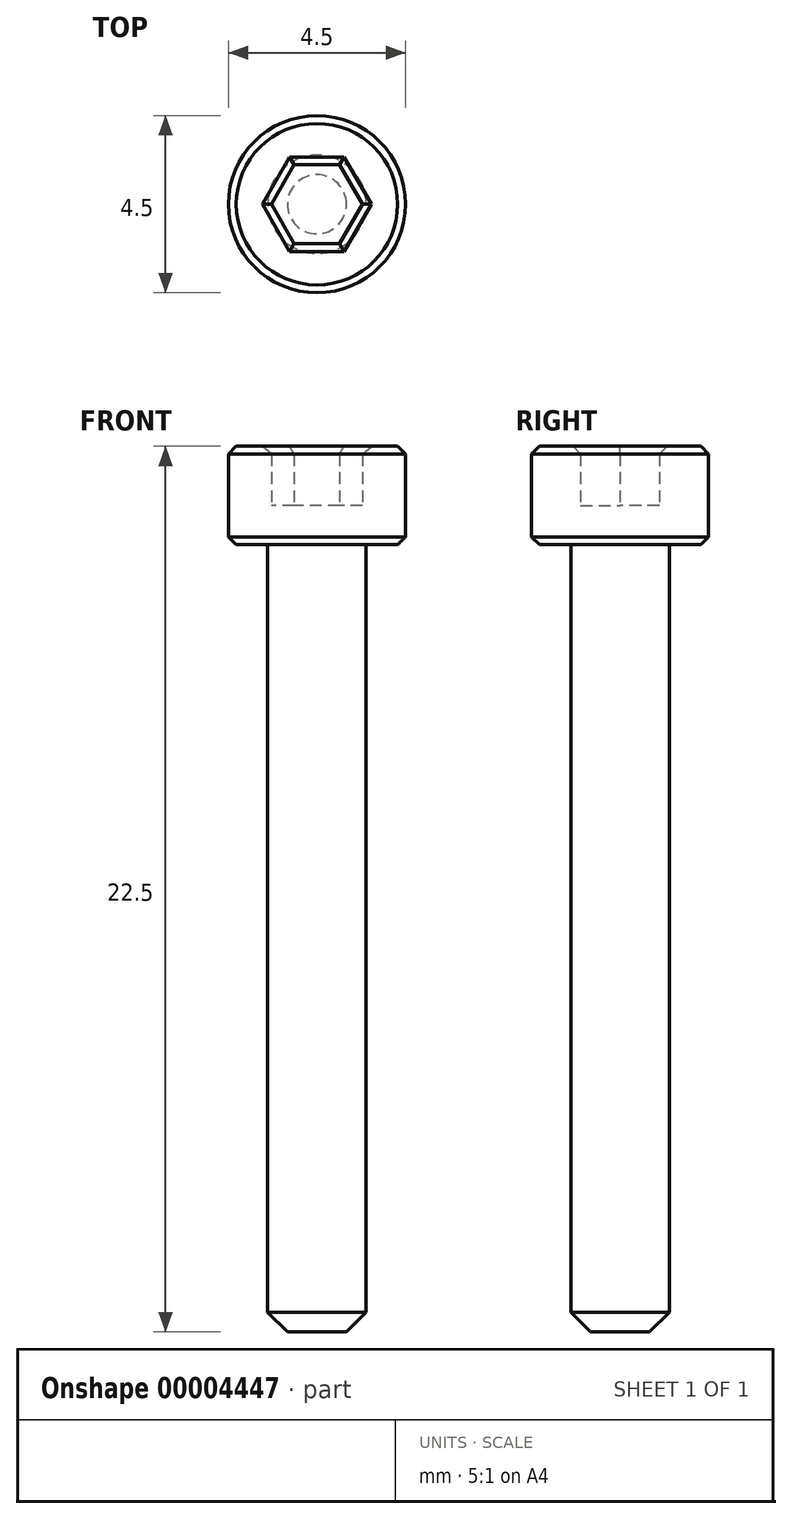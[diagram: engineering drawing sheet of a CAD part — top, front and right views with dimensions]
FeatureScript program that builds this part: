
annotation { "Feature Type Name" : "Feature", "Feature Type Description" : "" }
export const myFeature = defineFeature(function(context is Context, id is Id, definition is map)
    precondition{}
    {
        {
            var Q0;
            Q0=qCreatedBy(makeId("Top.planeOp"),FACE);
            var sketch = newSketch(context, id + "F0", { "sketchPlane" : qUnion([Q0])});
            skCircle(sketch, "E0", {"center": v(0, 0) * mm, "radius": 1.25 * mm});
            skCircle(sketch, "E1", {"center": v(0, 0) * mm, "radius": 2.25 * mm});
            skCircle(sketch, "E2.cCircle", {"center": v(0, 0) * mm, "radius": 1 * mm, "construction": true});
            skLineSegment(sketch, "E2.0", {"start": v(-0.58, 1) * mm, "end": v(0.58, 1) * mm});
            skLineSegment(sketch, "E2.1", {"start": v(0.58, 1) * mm, "end": v(1.15, 0) * mm});
            skLineSegment(sketch, "E2.2", {"start": v(1.15, 0) * mm, "end": v(0.58, -1) * mm});
            skLineSegment(sketch, "E2.3", {"start": v(0.58, -1) * mm, "end": v(-0.58, -1) * mm});
            skLineSegment(sketch, "E2.4", {"start": v(-0.58, -1) * mm, "end": v(-1.15, 0) * mm});
            skLineSegment(sketch, "E2.5", {"start": v(-1.15, 0) * mm, "end": v(-0.58, 1) * mm});
            skPoint(sketch, "E2.0.midPoint", {"position": v(0, 1) * mm});
            skSolve(sketch);
        }
        {
            var Q0;
            Q0=makeQuery(id+"F0.imprint","IMPRINT",FACE,{"disambiguationData":[TD([[makeQuery(id+"F0.imprint","IMPRINT",EDGE,{"derivedFrom":sQuery(id+"F0.wireOp",EDGE,"E0")}),-1.0]])]});
            var Q1;
            Q1=makeQuery(id+"F0.imprint","IMPRINT",FACE,{"disambiguationData":[TD([[makeQuery(id+"F0.imprint","IMPRINT",EDGE,{"derivedFrom":sQuery(id+"F0.wireOp",EDGE,"E0")}),1.0]])]});
            var Q2;
            Q2=makeQuery(id+"F0.imprint","IMPRINT",FACE,{"disambiguationData":[TD([[makeQuery(id+"F0.imprint","IMPRINT",EDGE,{"derivedFrom":sQuery(id+"F0.wireOp",EDGE,"E2.0")}),-1.0]])]});
            extrude(context, id + "F1", {"entities" : qUnion([Q0, Q1, Q2]), "depth" : 1 * mm});
        }
        {
            var Q0;
            Q0=makeQuery(id+"F0.imprint","IMPRINT",FACE,{"disambiguationData":[TD([[makeQuery(id+"F0.imprint","IMPRINT",EDGE,{"derivedFrom":sQuery(id+"F0.wireOp",EDGE,"E0")}),-1.0]])]});
            var Q1;
            Q1=makeQuery(id+"F0.imprint","IMPRINT",FACE,{"disambiguationData":[TD([[makeQuery(id+"F0.imprint","IMPRINT",EDGE,{"derivedFrom":sQuery(id+"F0.wireOp",EDGE,"E0")}),1.0]])]});
            extrude(context, id + "F2", {"entities" : qUnion([Q0, Q1]), "operationType" : NewBodyOperationType.ADD, "depth" : 2.5 * mm});
        }
        {
            var Q0;
            Q0=makeQuery(id+"F0.imprint","IMPRINT",FACE,{"disambiguationData":[TD([[makeQuery(id+"F0.imprint","IMPRINT",EDGE,{"derivedFrom":sQuery(id+"F0.wireOp",EDGE,"E0")}),1.0]])]});
            var Q1;
            Q1=makeQuery(id+"F0.imprint","IMPRINT",FACE,{"disambiguationData":[TD([[makeQuery(id+"F0.imprint","IMPRINT",EDGE,{"derivedFrom":sQuery(id+"F0.wireOp",EDGE,"E2.0")}),-1.0]])]});
            extrude(context, id + "F3", {"entities" : qUnion([Q0, Q1]), "operationType" : NewBodyOperationType.ADD, "oppositeDirection" : true, "depth" : 20 * mm});
        }
        {
            var Q0;
            Q0=makeQuery(id+"F3.opExtrude","CAP_EDGE",EDGE,{"disambiguationData":[OSD([sQuery(id+"F0.wireOp",EDGE,"E0")])],"isStart":false});
            chamfer(context, id + "F4", {"entities" : qUnion([Q0]), "width" : .5 * mm, "tangentPropagation" : true});
        }
        {
            var Q0;
            Q0=makeQuery(id+"F2.opExtrude","CAP_FACE",FACE,{"disambiguationData":[OSD([sQuery(id+"F0.wireOp",EDGE,"E1"),sQuery(id+"F0.wireOp",EDGE,"E2.0"),sQuery(id+"F0.wireOp",EDGE,"E2.1"),sQuery(id+"F0.wireOp",EDGE,"E2.2"),sQuery(id+"F0.wireOp",EDGE,"E2.3"),sQuery(id+"F0.wireOp",EDGE,"E2.4"),sQuery(id+"F0.wireOp",EDGE,"E2.5")])],"isStart":false});
            var Q1;
            Q1=makeQuery(id+"F1.opExtrude","CAP_EDGE",EDGE,{"disambiguationData":[OSD([sQuery(id+"F0.wireOp",EDGE,"E1")])],"isStart":true});
            chamfer(context, id + "F5", {"entities" : qUnion([Q0, Q1]), "width" : .2 * mm, "tangentPropagation" : true});
        }
    });
